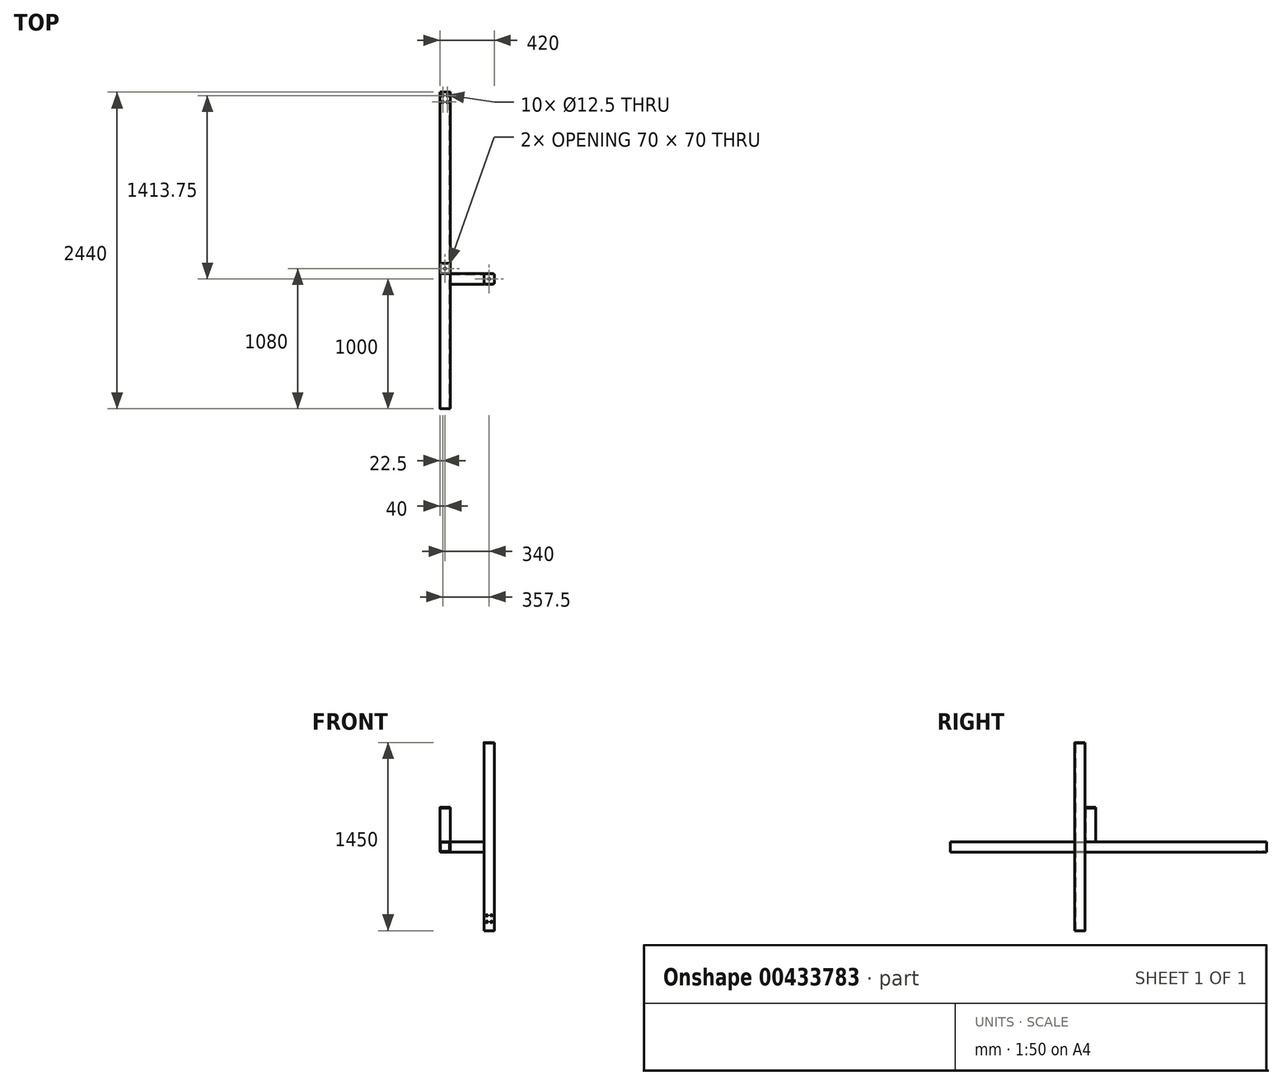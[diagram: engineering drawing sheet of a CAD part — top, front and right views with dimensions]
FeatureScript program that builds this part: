
annotation { "Feature Type Name" : "Feature", "Feature Type Description" : "" }
export const myFeature = defineFeature(function(context is Context, id is Id, definition is map)
    precondition{}
    {
        {
            var Q0;
            Q0=qCreatedBy(makeId("Top.planeOp"),FACE);
            var sketch = newSketch(context, id + "F0", { "sketchPlane" : qUnion([Q0])});
            skLineSegment(sketch, "E0.bottom", {"start": v(30, 40) * mm, "end": v(-30, 40) * mm});
            skLineSegment(sketch, "E0.top", {"start": v(30, -40) * mm, "end": v(-30, -40) * mm});
            skLineSegment(sketch, "E0.left", {"start": v(40, 30) * mm, "end": v(40, -30) * mm});
            skLineSegment(sketch, "E0.right", {"start": v(-40, 30) * mm, "end": v(-40, -30) * mm});
            skPoint(sketch, "E0.middle", {"position": v(0, 0) * mm});
            skPoint(sketch, "E1.visualSharp", {"position": v(-40, 40) * mm});
            skArc(sketch, "E1.filletArc", {"start": v(-30, 40) * mm, "mid": v(-37.07, 37.07) * mm, "end": v(-40, 30) * mm});
            skPoint(sketch, "E2.visualSharp", {"position": v(40, 40) * mm});
            skArc(sketch, "E2.filletArc", {"start": v(40, 30) * mm, "mid": v(37.07, 37.07) * mm, "end": v(30, 40) * mm});
            skPoint(sketch, "E3.visualSharp", {"position": v(40, -40) * mm});
            skArc(sketch, "E3.filletArc", {"start": v(30, -40) * mm, "mid": v(37.07, -37.07) * mm, "end": v(40, -30) * mm});
            skPoint(sketch, "E4.visualSharp", {"position": v(-40, -40) * mm});
            skArc(sketch, "E4.filletArc", {"start": v(-40, -30) * mm, "mid": v(-37.07, -37.07) * mm, "end": v(-30, -40) * mm});
            skArc(sketch, "E5.0", {"start": v(35, 30) * mm, "mid": v(33.54, 33.54) * mm, "end": v(30, 35) * mm});
            skLineSegment(sketch, "E5.1", {"start": v(35, 30) * mm, "end": v(35, -30) * mm});
            skLineSegment(sketch, "E5.2", {"start": v(30, 35) * mm, "end": v(-30, 35) * mm});
            skArc(sketch, "E5.3", {"start": v(30, -35) * mm, "mid": v(33.54, -33.54) * mm, "end": v(35, -30) * mm});
            skArc(sketch, "E5.4", {"start": v(-30, 35) * mm, "mid": v(-33.54, 33.54) * mm, "end": v(-35, 30) * mm});
            skLineSegment(sketch, "E5.5", {"start": v(-35, 30) * mm, "end": v(-35, -30) * mm});
            skArc(sketch, "E5.6", {"start": v(-35, -30) * mm, "mid": v(-33.54, -33.54) * mm, "end": v(-30, -35) * mm});
            skLineSegment(sketch, "E5.7", {"start": v(30, -35) * mm, "end": v(-30, -35) * mm});
            skSolve(sketch);
        }
        {
            var Q0;
            Q0=makeQuery(id+"F0.imprint","IMPRINT",FACE,{"disambiguationData":[TD([[makeQuery(id+"F0.imprint","IMPRINT",EDGE,{"derivedFrom":sQuery(id+"F0.wireOp",EDGE,"E0.bottom")}),1.0]])]});
            var Q1;
            Q1=qConstructionFilter(qBodyType(qCreatedBy(id+"F0",EDGE),BodyType.WIRE),ConstructionObject.NO);
            extrude(context, id + "F1", {"entities" : qUnion([Q0]), "surfaceEntities" : qUnion([Q1]), "depth" : 1445 * mm});
        }
        {
            var Q0;
            Q0=makeQuery(id+"F1.opExtrude","SWEPT_FACE",FACE,{"disambiguationData":[OSD([sQuery(id+"F0.wireOp",EDGE,"E0.right")])]});
            var sketch = newSketch(context, id + "F2", { "sketchPlane" : qUnion([Q0])});
            skLineSegment(sketch, "E6", {"start": v(0, 1445) * mm, "end": v(0, 0) * mm, "construction": true});
            skLineSegment(sketch, "E7.bottom", {"start": v(30, 685) * mm, "end": v(-30, 685) * mm});
            skLineSegment(sketch, "E7.top", {"start": v(30, 605) * mm, "end": v(-30, 605) * mm});
            skLineSegment(sketch, "E7.left", {"start": v(40, 675) * mm, "end": v(40, 615) * mm});
            skLineSegment(sketch, "E7.right", {"start": v(-40, 675) * mm, "end": v(-40, 615) * mm});
            skPoint(sketch, "E7.middle", {"position": v(0, 645) * mm});
            skPoint(sketch, "E8.visualSharp", {"position": v(-40, 685) * mm});
            skArc(sketch, "E8.filletArc", {"start": v(-30, 685) * mm, "mid": v(-37.07, 682.07) * mm, "end": v(-40, 675) * mm});
            skPoint(sketch, "E9.visualSharp", {"position": v(40, 685) * mm});
            skArc(sketch, "E9.filletArc", {"start": v(40, 675) * mm, "mid": v(37.07, 682.07) * mm, "end": v(30, 685) * mm});
            skPoint(sketch, "E10.visualSharp", {"position": v(40, 605) * mm});
            skArc(sketch, "E10.filletArc", {"start": v(30, 605) * mm, "mid": v(37.07, 607.93) * mm, "end": v(40, 615) * mm});
            skPoint(sketch, "E11.visualSharp", {"position": v(-40, 605) * mm});
            skArc(sketch, "E11.filletArc", {"start": v(-40, 615) * mm, "mid": v(-37.07, 607.93) * mm, "end": v(-30, 605) * mm});
            skArc(sketch, "E12.0", {"start": v(35, 675) * mm, "mid": v(33.54, 678.54) * mm, "end": v(30, 680) * mm});
            skLineSegment(sketch, "E12.1", {"start": v(35, 675) * mm, "end": v(35, 615) * mm});
            skLineSegment(sketch, "E12.2", {"start": v(30, 680) * mm, "end": v(-30, 680) * mm});
            skArc(sketch, "E12.3", {"start": v(30, 610) * mm, "mid": v(33.54, 611.46) * mm, "end": v(35, 615) * mm});
            skArc(sketch, "E12.4", {"start": v(-30, 680) * mm, "mid": v(-33.54, 678.54) * mm, "end": v(-35, 675) * mm});
            skLineSegment(sketch, "E12.5", {"start": v(-35, 675) * mm, "end": v(-35, 615) * mm});
            skArc(sketch, "E12.6", {"start": v(-35, 615) * mm, "mid": v(-33.54, 611.46) * mm, "end": v(-30, 610) * mm});
            skLineSegment(sketch, "E12.7", {"start": v(30, 610) * mm, "end": v(-30, 610) * mm});
            skSolve(sketch);
        }
        {
            var Q0;
            Q0=qSketchRegion(id+"F2",true);
            extrude(context, id + "F3", {"entities" : qUnion([Q0]), "depth" : 260 * mm});
        }
        {
            var Q0;
            Q0=qCreatedBy(makeId("Front.planeOp"),FACE);
            var sketch = newSketch(context, id + "F4", { "sketchPlane" : qUnion([Q0])});
            skLineSegment(sketch, "E13.bottom", {"start": v(-370, 685) * mm, "end": v(-310, 685) * mm});
            skLineSegment(sketch, "E13.top", {"start": v(-370, 605) * mm, "end": v(-310, 605) * mm});
            skLineSegment(sketch, "E13.left", {"start": v(-380, 675) * mm, "end": v(-380, 615) * mm});
            skLineSegment(sketch, "E13.right", {"start": v(-300, 675) * mm, "end": v(-300, 615) * mm});
            skPoint(sketch, "E13.middle", {"position": v(-340, 645) * mm});
            skPoint(sketch, "E14.visualSharp", {"position": v(-300, 685) * mm});
            skArc(sketch, "E14.filletArc", {"start": v(-300, 675) * mm, "mid": v(-302.93, 682.07) * mm, "end": v(-310, 685) * mm});
            skPoint(sketch, "E15.visualSharp", {"position": v(-380, 685) * mm});
            skArc(sketch, "E15.filletArc", {"start": v(-370, 685) * mm, "mid": v(-377.07, 682.07) * mm, "end": v(-380, 675) * mm});
            skPoint(sketch, "E16.visualSharp", {"position": v(-380, 605) * mm});
            skArc(sketch, "E16.filletArc", {"start": v(-380, 615) * mm, "mid": v(-377.07, 607.93) * mm, "end": v(-370, 605) * mm});
            skPoint(sketch, "E17.visualSharp", {"position": v(-300, 605) * mm});
            skArc(sketch, "E17.filletArc", {"start": v(-310, 605) * mm, "mid": v(-302.93, 607.93) * mm, "end": v(-300, 615) * mm});
            skArc(sketch, "E18.0", {"start": v(-370, 680) * mm, "mid": v(-373.54, 678.54) * mm, "end": v(-375, 675) * mm});
            skLineSegment(sketch, "E18.1", {"start": v(-375, 675) * mm, "end": v(-375, 615) * mm});
            skLineSegment(sketch, "E18.2", {"start": v(-370, 680) * mm, "end": v(-310, 680) * mm});
            skArc(sketch, "E18.3", {"start": v(-375, 615) * mm, "mid": v(-373.54, 611.46) * mm, "end": v(-370, 610) * mm});
            skArc(sketch, "E18.4", {"start": v(-305, 675) * mm, "mid": v(-306.46, 678.54) * mm, "end": v(-310, 680) * mm});
            skLineSegment(sketch, "E18.5", {"start": v(-305, 675) * mm, "end": v(-305, 615) * mm});
            skArc(sketch, "E18.6", {"start": v(-310, 610) * mm, "mid": v(-306.46, 611.46) * mm, "end": v(-305, 615) * mm});
            skLineSegment(sketch, "E18.7", {"start": v(-370, 610) * mm, "end": v(-310, 610) * mm});
            skSolve(sketch);
        }
        {
            var Q0;
            Q0=qSketchRegion(id+"F4",true);
            extrude(context, id + "F5", {"entities" : qUnion([Q0]), "depth" : 1000 * mm, "hasSecondDirection" : true, "secondDirectionOppositeDirection" : true, "secondDirectionDepth" : 1440 * mm});
        }
        {
            var Q0;
            Q0=makeQuery(id+"F5.opExtrude","SWEPT_FACE",FACE,{"disambiguationData":[OSD([sQuery(id+"F4.wireOp",EDGE,"E13.bottom")])]});
            var sketch = newSketch(context, id + "F6", { "sketchPlane" : qUnion([Q0])});
            skCircle(sketch, "E19", {"center": v(-357.5, 1413.75) * mm, "radius": 6.25 * mm});
            skLineSegment(sketch, "E20", {"start": v(-340, 1440) * mm, "end": v(-340, 1279.9) * mm, "construction": true});
            skCircle(sketch, "E21.0.1.0", {"center": v(-357.5, 1363.75) * mm, "radius": 6.25 * mm});
            skLineSegment(sketch, "E21.direction1", {"start": v(-425, 1413.75) * mm, "end": v(-357.5, 1413.75) * mm, "construction": true});
            skLineSegment(sketch, "E21.direction2", {"start": v(-357.5, 1413.75) * mm, "end": v(-357.5, 1363.75) * mm, "construction": true});
            skCircle(sketch, "E22.MirrorC", {"center": v(-322.5, 1363.75) * mm, "radius": 6.25 * mm});
            skCircle(sketch, "E23.MirrorC", {"center": v(-322.5, 1413.75) * mm, "radius": 6.25 * mm});
            skSolve(sketch);
        }
        {
            var Q0;
            Q0 = qSketchRegion(id + "F6", true);
            extrude(context, id + "F7", {"entities" : qUnion([Q0]), "operationType" : NewBodyOperationType.REMOVE, "endBound" : BoundingType.THROUGH_ALL, "oppositeDirection" : true, "depth" : 25 * mm});
        }
        {
            var Q0;
            Q0=makeQuery(id+"F1.opExtrude","SWEPT_FACE",FACE,{"disambiguationData":[OSD([sQuery(id+"F0.wireOp",EDGE,"E0.top")])]});
            var sketch = newSketch(context, id + "F8", { "sketchPlane" : qUnion([Q0])});
            skLineSegment(sketch, "E24", {"start": v(0, 0) * mm, "end": v(0, 14) * mm, "construction": true});
            skCircle(sketch, "E25", {"center": v(-17.5, 117.5) * mm, "radius": 6.25 * mm});
            skCircle(sketch, "E26", {"center": v(-17.5, 67.5) * mm, "radius": 6.25 * mm});
            skCircle(sketch, "E27.MirrorC", {"center": v(17.5, 67.5) * mm, "radius": 6.25 * mm});
            skCircle(sketch, "E28.MirrorC", {"center": v(17.5, 117.5) * mm, "radius": 6.25 * mm});
            skSolve(sketch);
        }
        {
            var Q0;
            Q0 = qSketchRegion(id + "F8", true);
            extrude(context, id + "F9", {"entities" : qUnion([Q0]), "operationType" : NewBodyOperationType.REMOVE, "endBound" : BoundingType.THROUGH_ALL, "oppositeDirection" : true, "depth" : 25 * mm});
        }
        {
            var Q0;
            Q0=makeQuery(id+"F1.opExtrude","CAP_FACE",FACE,{"disambiguationData":[OSD([sQuery(id+"F0.wireOp",EDGE,"E0.bottom"),sQuery(id+"F0.wireOp",EDGE,"E0.top"),sQuery(id+"F0.wireOp",EDGE,"E0.left"),sQuery(id+"F0.wireOp",EDGE,"E0.right"),sQuery(id+"F0.wireOp",EDGE,"E1.filletArc"),sQuery(id+"F0.wireOp",EDGE,"E2.filletArc"),sQuery(id+"F0.wireOp",EDGE,"E3.filletArc"),sQuery(id+"F0.wireOp",EDGE,"E4.filletArc"),sQuery(id+"F0.wireOp",EDGE,"E5.0"),sQuery(id+"F0.wireOp",EDGE,"E5.1"),sQuery(id+"F0.wireOp",EDGE,"E5.2"),sQuery(id+"F0.wireOp",EDGE,"E5.3"),sQuery(id+"F0.wireOp",EDGE,"E5.4"),sQuery(id+"F0.wireOp",EDGE,"E5.5"),sQuery(id+"F0.wireOp",EDGE,"E5.6"),sQuery(id+"F0.wireOp",EDGE,"E5.7")])],"isStart":false});
            var sketch = newSketch(context, id + "F10", { "sketchPlane" : qUnion([Q0])});
            skArc(sketch, "E29.0", {"start": v(-30, 40) * mm, "mid": v(-37.07, 37.07) * mm, "end": v(-40, 30) * mm});
            skLineSegment(sketch, "E29.1", {"start": v(30, 40) * mm, "end": v(-30, 40) * mm});
            skLineSegment(sketch, "E29.2", {"start": v(-40, 30) * mm, "end": v(-40, -30) * mm});
            skArc(sketch, "E29.3", {"start": v(-40, -30) * mm, "mid": v(-37.07, -37.07) * mm, "end": v(-30, -40) * mm});
            skLineSegment(sketch, "E29.4", {"start": v(30, -40) * mm, "end": v(-30, -40) * mm});
            skArc(sketch, "E29.5", {"start": v(30, -40) * mm, "mid": v(37.07, -37.07) * mm, "end": v(40, -30) * mm});
            skLineSegment(sketch, "E29.6", {"start": v(40, 30) * mm, "end": v(40, -30) * mm});
            skArc(sketch, "E29.7", {"start": v(40, 30) * mm, "mid": v(37.07, 37.07) * mm, "end": v(30, 40) * mm});
            skCircle(sketch, "E30", {"center": v(0, 0) * mm, "radius": 6.25 * mm});
            skSolve(sketch);
        }
        {
            var Q0;
            Q0 = qSketchRegion(id + "F10", true);
            extrude(context, id + "F11", {"entities" : qUnion([Q0]), "depth" : 5 * mm});
        }
        {
            var Q0;
            Q0=makeQuery(id+"F5.opExtrude","SWEPT_FACE",FACE,{"disambiguationData":[OSD([sQuery(id+"F4.wireOp",EDGE,"E13.bottom")])]});
            var sketch = newSketch(context, id + "F12", { "sketchPlane" : qUnion([Q0])});
            skLineSegment(sketch, "E31.bottom", {"start": v(-310, 120) * mm, "end": v(-370, 120) * mm});
            skLineSegment(sketch, "E31.top", {"start": v(-310, 40) * mm, "end": v(-370, 40) * mm});
            skLineSegment(sketch, "E31.left", {"start": v(-300, 110) * mm, "end": v(-300, 50) * mm});
            skLineSegment(sketch, "E31.right", {"start": v(-380, 110) * mm, "end": v(-380, 50) * mm});
            skPoint(sketch, "E31.middle", {"position": v(-340, 80) * mm});
            skPoint(sketch, "E32.visualSharp", {"position": v(-300, 120) * mm});
            skArc(sketch, "E32.filletArc", {"start": v(-300, 110) * mm, "mid": v(-302.93, 117.07) * mm, "end": v(-310, 120) * mm});
            skPoint(sketch, "E33.visualSharp", {"position": v(-380, 120) * mm});
            skArc(sketch, "E33.filletArc", {"start": v(-370, 120) * mm, "mid": v(-377.07, 117.07) * mm, "end": v(-380, 110) * mm});
            skPoint(sketch, "E34.visualSharp", {"position": v(-380, 40) * mm});
            skArc(sketch, "E34.filletArc", {"start": v(-380, 50) * mm, "mid": v(-377.07, 42.93) * mm, "end": v(-370, 40) * mm});
            skPoint(sketch, "E35.visualSharp", {"position": v(-300, 40) * mm});
            skArc(sketch, "E35.filletArc", {"start": v(-310, 40) * mm, "mid": v(-302.93, 42.93) * mm, "end": v(-300, 50) * mm});
            skArc(sketch, "E36.0", {"start": v(-305, 110) * mm, "mid": v(-306.46, 113.54) * mm, "end": v(-310, 115) * mm});
            skLineSegment(sketch, "E36.1", {"start": v(-305, 110) * mm, "end": v(-305, 50) * mm});
            skLineSegment(sketch, "E36.2", {"start": v(-310, 115) * mm, "end": v(-370, 115) * mm});
            skArc(sketch, "E36.3", {"start": v(-310, 45) * mm, "mid": v(-306.46, 46.46) * mm, "end": v(-305, 50) * mm});
            skArc(sketch, "E36.4", {"start": v(-370, 115) * mm, "mid": v(-373.54, 113.54) * mm, "end": v(-375, 110) * mm});
            skLineSegment(sketch, "E36.5", {"start": v(-375, 110) * mm, "end": v(-375, 50) * mm});
            skArc(sketch, "E36.6", {"start": v(-375, 50) * mm, "mid": v(-373.54, 46.46) * mm, "end": v(-370, 45) * mm});
            skLineSegment(sketch, "E36.7", {"start": v(-310, 45) * mm, "end": v(-370, 45) * mm});
            skSolve(sketch);
        }
        {
            var Q0;
            Q0 = qSketchRegion(id + "F12", true);
            extrude(context, id + "F13", {"entities" : qUnion([Q0]), "depth" : 260 * mm});
        }
        {
            var Q0;
            Q0=makeQuery(id+"F13.opExtrude","CAP_FACE",FACE,{"disambiguationData":[OSD([sQuery(id+"F12.wireOp",EDGE,"E31.bottom"),sQuery(id+"F12.wireOp",EDGE,"E31.top"),sQuery(id+"F12.wireOp",EDGE,"E31.left"),sQuery(id+"F12.wireOp",EDGE,"E31.right"),sQuery(id+"F12.wireOp",EDGE,"E32.filletArc"),sQuery(id+"F12.wireOp",EDGE,"E33.filletArc"),sQuery(id+"F12.wireOp",EDGE,"E34.filletArc"),sQuery(id+"F12.wireOp",EDGE,"E35.filletArc"),sQuery(id+"F12.wireOp",EDGE,"E36.0"),sQuery(id+"F12.wireOp",EDGE,"E36.1"),sQuery(id+"F12.wireOp",EDGE,"E36.2"),sQuery(id+"F12.wireOp",EDGE,"E36.3"),sQuery(id+"F12.wireOp",EDGE,"E36.4"),sQuery(id+"F12.wireOp",EDGE,"E36.5"),sQuery(id+"F12.wireOp",EDGE,"E36.6"),sQuery(id+"F12.wireOp",EDGE,"E36.7")])],"isStart":false});
            var sketch = newSketch(context, id + "F14", { "sketchPlane" : qUnion([Q0])});
            skLineSegment(sketch, "E37.0", {"start": v(-310, 120) * mm, "end": v(-370, 120) * mm});
            skArc(sketch, "E37.1", {"start": v(-370, 120) * mm, "mid": v(-377.07, 117.07) * mm, "end": v(-380, 110) * mm});
            skLineSegment(sketch, "E37.2", {"start": v(-380, 110) * mm, "end": v(-380, 50) * mm});
            skArc(sketch, "E37.3", {"start": v(-380, 50) * mm, "mid": v(-377.07, 42.93) * mm, "end": v(-370, 40) * mm});
            skLineSegment(sketch, "E37.4", {"start": v(-310, 40) * mm, "end": v(-370, 40) * mm});
            skArc(sketch, "E37.5", {"start": v(-310, 40) * mm, "mid": v(-302.93, 42.93) * mm, "end": v(-300, 50) * mm});
            skLineSegment(sketch, "E37.6", {"start": v(-300, 110) * mm, "end": v(-300, 50) * mm});
            skArc(sketch, "E37.7", {"start": v(-300, 110) * mm, "mid": v(-302.93, 117.07) * mm, "end": v(-310, 120) * mm});
            skCircle(sketch, "E38", {"center": v(-340, 80) * mm, "radius": 6.25 * mm});
            skPoint(sketch, "E38.centerSnap0", {"position": v(-300, 80) * mm});
            skPoint(sketch, "E38.centerSnap1", {"position": v(-340, 120) * mm});
            skSolve(sketch);
        }
        {
            var Q0;
            Q0 = qSketchRegion(id + "F14", true);
            extrude(context, id + "F15", {"entities" : qUnion([Q0]), "depth" : 5 * mm});
        }
    });
